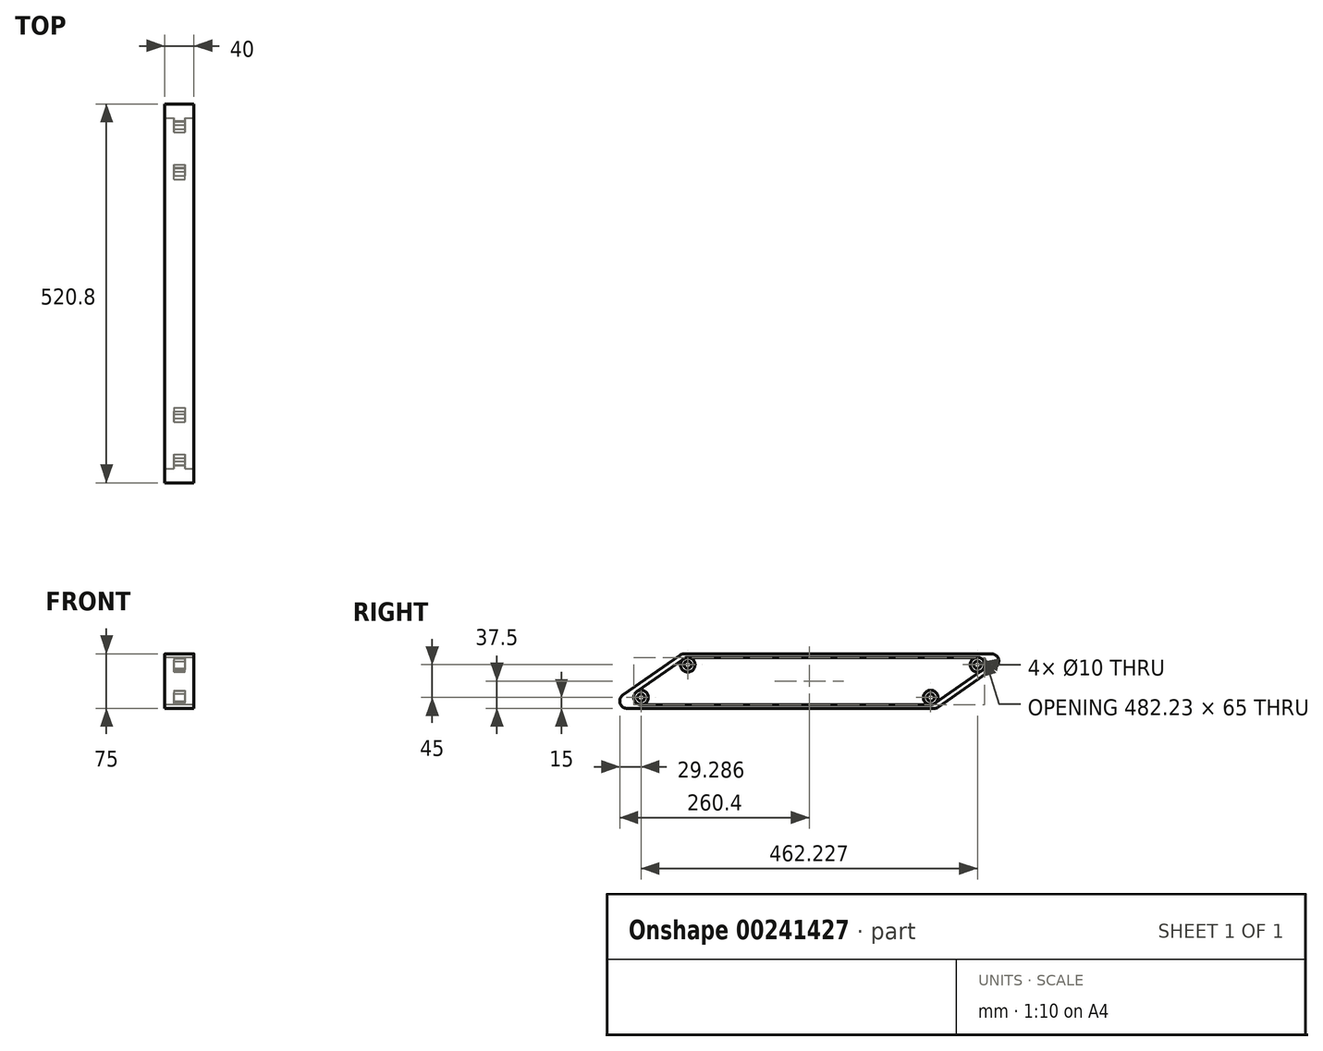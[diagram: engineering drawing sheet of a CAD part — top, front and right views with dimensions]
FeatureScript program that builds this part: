
annotation { "Feature Type Name" : "Feature", "Feature Type Description" : "" }
export const myFeature = defineFeature(function(context is Context, id is Id, definition is map)
    precondition{}
    {
        {
            var Q0;
            Q0=qCreatedBy(makeId("Right.planeOp"),FACE);
            cPlane(context, id + "F0", {"entities" : qUnion([Q0]), "cplaneType" : CPlaneType.OFFSET, "offset" : 20 * mm, "width" : 150 * mm, "height" : 150 * mm});
        }
        {
            var Q0;
            Q0=qCreatedBy(makeId("Right.planeOp"),FACE);
            var sketch = newSketch(context, id + "F1", { "sketchPlane" : qUnion([Q0])});
            skLineSegment(sketch, "E0.bottom", {"start": v(175, 37.5) * mm, "end": v(-175, 37.5) * mm});
            skLineSegment(sketch, "E0.top", {"start": v(175, -37.5) * mm, "end": v(-175, -37.5) * mm});
            skLineSegment(sketch, "E0.left", {"start": v(175, 37.5) * mm, "end": v(175, -37.5) * mm});
            skLineSegment(sketch, "E0.right", {"start": v(-175, 37.5) * mm, "end": v(-175, -37.5) * mm});
            skPoint(sketch, "E0.middle", {"position": v(0, 0) * mm});
            skLineSegment(sketch, "E1", {"start": v(175, -37.5) * mm, "end": v(282.11, 37.5) * mm});
            skLineSegment(sketch, "E2", {"start": v(282.11, 37.5) * mm, "end": v(175, 37.5) * mm});
            skLineSegment(sketch, "E3", {"start": v(-175, 37.5) * mm, "end": v(-282.11, -37.5) * mm});
            skLineSegment(sketch, "E4", {"start": v(-282.11, -37.5) * mm, "end": v(-175, -37.5) * mm});
            skLineSegment(sketch, "E5.bottom", {"start": v(170, 32.5) * mm, "end": v(-170, 32.5) * mm});
            skLineSegment(sketch, "E5.top", {"start": v(170, -32.5) * mm, "end": v(-170, -32.5) * mm});
            skLineSegment(sketch, "E5.left", {"start": v(170, 32.5) * mm, "end": v(170, -32.5) * mm});
            skLineSegment(sketch, "E5.right", {"start": v(-170, 32.5) * mm, "end": v(-170, -32.5) * mm});
            skLineSegment(sketch, "E6", {"start": v(170, -32.5) * mm, "end": v(262.83, 32.5) * mm});
            skLineSegment(sketch, "E7", {"start": v(262.83, 32.5) * mm, "end": v(170, 32.5) * mm});
            skLineSegment(sketch, "E8", {"start": v(-170, 32.5) * mm, "end": v(-262.83, -32.5) * mm});
            skLineSegment(sketch, "E9", {"start": v(-262.83, -32.5) * mm, "end": v(-170, -32.5) * mm});
            skSolve(sketch);
        }
        {
            var Q0;
            Q0 = qSketchRegion(id + "F1", true);
            extrude(context, id + "F2", {"entities" : qUnion([Q0]), "depth" : 40 * mm});
        }
        {
            var Q0;
            Q0=makeQuery(id+"F2.opExtrude","SWEPT_EDGE",EDGE,{"disambiguationData":[OSD([sQuery(id+"F1.wireOp",EDGE,"E1"),sQuery(id+"F1.wireOp",EDGE,"E2")])]});
            var Q1;
            Q1=makeQuery(id+"F2.opExtrude","SWEPT_EDGE",EDGE,{"disambiguationData":[OSD([sQuery(id+"F1.wireOp",EDGE,"E6"),sQuery(id+"F1.wireOp",EDGE,"E7")])]});
            var Q2;
            Q2=makeQuery(id+"F2.opExtrude","SWEPT_EDGE",EDGE,{"disambiguationData":[OSD([sQuery(id+"F1.wireOp",EDGE,"E5.top"),sQuery(id+"F1.wireOp",EDGE,"E5.left"),sQuery(id+"F1.wireOp",EDGE,"E6")])]});
            var Q3;
            Q3=makeQuery(id+"F2.opExtrude","SWEPT_EDGE",EDGE,{"disambiguationData":[OSD([sQuery(id+"F1.wireOp",EDGE,"E3"),sQuery(id+"F1.wireOp",EDGE,"E4")])]});
            var Q4;
            Q4=makeQuery(id+"F2.opExtrude","SWEPT_EDGE",EDGE,{"disambiguationData":[OSD([sQuery(id+"F1.wireOp",EDGE,"E0.bottom"),sQuery(id+"F1.wireOp",EDGE,"E0.right"),sQuery(id+"F1.wireOp",EDGE,"E3")])]});
            var Q5;
            Q5=makeQuery(id+"F2.opExtrude","SWEPT_EDGE",EDGE,{"disambiguationData":[OSD([sQuery(id+"F1.wireOp",EDGE,"E5.bottom"),sQuery(id+"F1.wireOp",EDGE,"E5.right"),sQuery(id+"F1.wireOp",EDGE,"E8")])]});
            var Q6;
            Q6=makeQuery(id+"F2.opExtrude","SWEPT_EDGE",EDGE,{"disambiguationData":[OSD([sQuery(id+"F1.wireOp",EDGE,"E8"),sQuery(id+"F1.wireOp",EDGE,"E9")])]});
            var Q7;
            Q7=makeQuery(id+"F2.opExtrude","SWEPT_EDGE",EDGE,{"disambiguationData":[OSD([sQuery(id+"F1.wireOp",EDGE,"E0.top"),sQuery(id+"F1.wireOp",EDGE,"E0.left"),sQuery(id+"F1.wireOp",EDGE,"E1")])]});
            fillet(context, id + "F3", {"entities" : qUnion([Q0, Q1, Q2, Q3, Q4, Q5, Q6, Q7]), "radius" : 10 * mm, "tangentPropagation" : true, "allowEdgeOverflow" : false});
        }
        {
            var Q0;
            Q0=qCreatedBy(id+"F0.planeOp",FACE);
            var sketch = newSketch(context, id + "F4", { "sketchPlane" : qUnion([Q0])});
            skCircle(sketch, "E10", {"center": v(-166.85, 22.5) * mm, "radius": 10 * mm});
            skCircle(sketch, "E11", {"center": v(-231.11, -22.5) * mm, "radius": 10 * mm});
            skCircle(sketch, "E12", {"center": v(166.85, -22.5) * mm, "radius": 10 * mm});
            skCircle(sketch, "E13", {"center": v(231.11, 22.5) * mm, "radius": 10 * mm});
            skCircle(sketch, "E14", {"center": v(-166.85, 22.5) * mm, "radius": 5 * mm});
            skCircle(sketch, "E15", {"center": v(-231.11, -22.5) * mm, "radius": 5 * mm});
            skCircle(sketch, "E16", {"center": v(231.11, 22.5) * mm, "radius": 5 * mm});
            skCircle(sketch, "E17", {"center": v(166.85, -22.5) * mm, "radius": 5 * mm});
            skSolve(sketch);
        }
        {
            var Q0;
            Q0 = qSketchRegion(id + "F4", true);
            extrude(context, id + "F5", {"entities" : qUnion([Q0]), "operationType" : NewBodyOperationType.ADD, "endBound" : BoundingType.SYMMETRIC, "oppositeDirection" : true, "depth" : 15 * mm});
        }
    });
